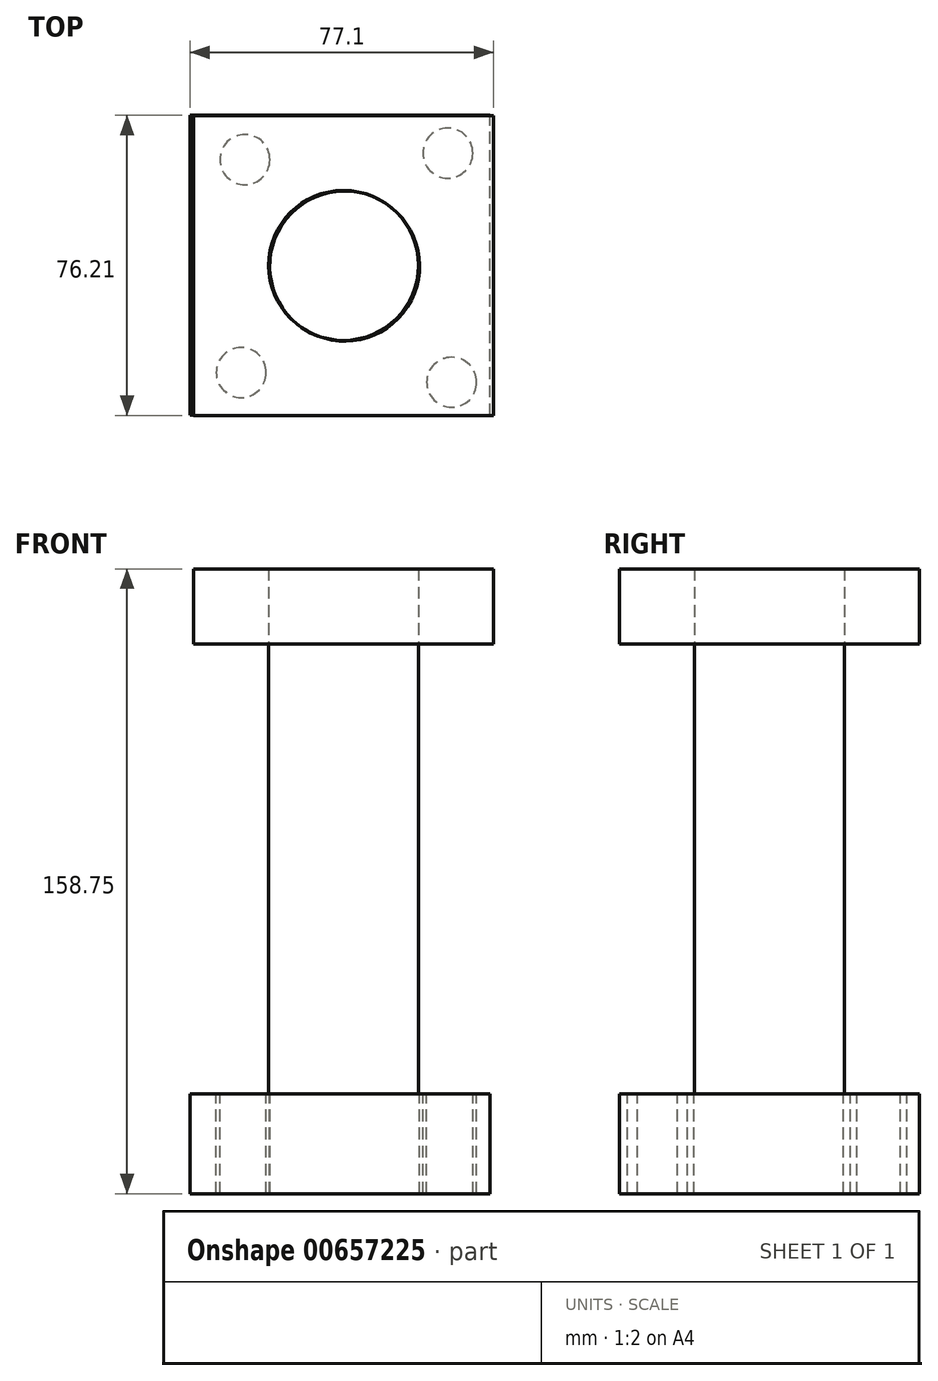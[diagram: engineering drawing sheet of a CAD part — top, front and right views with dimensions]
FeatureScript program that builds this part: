
annotation { "Feature Type Name" : "Feature", "Feature Type Description" : "" }
export const myFeature = defineFeature(function(context is Context, id is Id, definition is map)
    precondition{}
    {
        {
            var Q0;
            Q0=qCreatedBy(makeId("Top.planeOp"),FACE);
            var sketch = newSketch(context, id + "F0", { "sketchPlane" : qUnion([Q0])});
            skLineSegment(sketch, "E0.bottom", {"start": v(16.86, -50.22) * mm, "end": v(93.06, -50.22) * mm});
            skLineSegment(sketch, "E0.top", {"start": v(16.86, 25.98) * mm, "end": v(93.06, 25.98) * mm});
            skLineSegment(sketch, "E0.left", {"start": v(16.86, -50.22) * mm, "end": v(16.86, 25.98) * mm});
            skLineSegment(sketch, "E0.right", {"start": v(93.06, -50.22) * mm, "end": v(93.06, 25.98) * mm});
            skPoint(sketch, "E0.middle", {"position": v(54.96, -12.12) * mm});
            skSolve(sketch);
        }
        {
            var Q0;
            Q0 = qSketchRegion(id + "F0", true);
            extrude(context, id + "F1", {"entities" : qUnion([Q0]), "depth" : 25.4 * mm, "offsetDistance" : 25.4 * mm});
        }
        {
            var Q0;
            Q0=makeQuery(id+"F1.opExtrude","CAP_FACE",FACE,{"disambiguationData":[OSD([sQuery(id+"F0.wireOp",EDGE,"E0.bottom"),sQuery(id+"F0.wireOp",EDGE,"E0.top"),sQuery(id+"F0.wireOp",EDGE,"E0.left"),sQuery(id+"F0.wireOp",EDGE,"E0.right")])],"isStart":false});
            var sketch = newSketch(context, id + "F2", { "sketchPlane" : qUnion([Q0])});
            skCircle(sketch, "E1", {"center": v(56.15, -12.32) * mm, "radius": 19.05 * mm});
            skSolve(sketch);
        }
        {
            var Q0;
            Q0=makeQuery(id+"F2.imprint","IMPRINT",FACE,{"disambiguationData":[TD([[makeQuery(id+"F2.imprint","IMPRINT",EDGE,{"derivedFrom":sQuery(id+"F2.wireOp",EDGE,"E1")}),-1.0]])]});
            var sketch = newSketch(context, id + "F3", { "sketchPlane" : qUnion([Q0])});
            skSolve(sketch);
        }
        {
            var Q0;
            Q0=sQuery(id+"F2.wireOp",VERTEX,"E1.center");
            var Q1;
            Q1=makeQuery(id+"F1.opExtrude","SWEPT_BODY",BODY,{"disambiguationData":[OSD([sQuery(id+"F0.wireOp",EDGE,"E0.bottom"),sQuery(id+"F0.wireOp",EDGE,"E0.top"),sQuery(id+"F0.wireOp",EDGE,"E0.left"),sQuery(id+"F0.wireOp",EDGE,"E0.right")])]});
            hole(context, id + "F4", {"style" : HoleStyle.SIMPLE, "endStyle" : HoleEndStyle.THROUGH, "holeDiameter" : 38.1 * mm, "majorDiameter" : 6.35 * mm, "isTappedThrough" : true, "tappedDepth" : 12.7 * mm, "tapClearance" : 3, "locations" : qUnion([Q0]), "scope" : qUnion([Q1])});
        }
        {
            var Q0;
            Q0=makeQuery(id+"F3.imprint","IMPRINT",FACE,{"disambiguationData":[TD([[makeQuery(id+"F3.imprint","IMPRINT",EDGE,{"derivedFrom":makeQuery(id+"F2.imprint","IMPRINT",EDGE,{"derivedFrom":sQuery(id+"F2.wireOp",EDGE,"E1")})}),-1.0]])]});
            var sketch = newSketch(context, id + "F5", { "sketchPlane" : qUnion([Q0])});
            skCircle(sketch, "E2", {"center": v(82.35, 16.4) * mm, "radius": 4.88 * mm});
            skSolve(sketch);
        }
        {
            var Q0;
            Q0=makeQuery(id+"F5.imprint","IMPRINT",FACE,{"disambiguationData":[TD([[makeQuery(id+"F5.imprint","IMPRINT",EDGE,{"derivedFrom":sQuery(id+"F5.wireOp",EDGE,"E2")}),-1.0]])]});
            var sketch = newSketch(context, id + "F6", { "sketchPlane" : qUnion([Q0])});
            skCircle(sketch, "E3", {"center": v(83.35, -41.82) * mm, "radius": 4.75 * mm});
            skSolve(sketch);
        }
        {
            var Q0;
            Q0=makeQuery(id+"F3.imprint","IMPRINT",FACE,{"disambiguationData":[TD([[makeQuery(id+"F3.imprint","IMPRINT",EDGE,{"derivedFrom":makeQuery(id+"F2.imprint","IMPRINT",EDGE,{"derivedFrom":sQuery(id+"F2.wireOp",EDGE,"E1")})}),-1.0]])]});
            var sketch = newSketch(context, id + "F7", { "sketchPlane" : qUnion([Q0])});
            skCircle(sketch, "E4", {"center": v(29.88, -39.36) * mm, "radius": 5.21 * mm});
            skSolve(sketch);
        }
        {
            var Q0;
            Q0=makeQuery(id+"F3.imprint","IMPRINT",FACE,{"disambiguationData":[TD([[makeQuery(id+"F3.imprint","IMPRINT",EDGE,{"derivedFrom":makeQuery(id+"F2.imprint","IMPRINT",EDGE,{"derivedFrom":sQuery(id+"F2.wireOp",EDGE,"E1")})}),-1.0]])]});
            var sketch = newSketch(context, id + "F8", { "sketchPlane" : qUnion([Q0])});
            skCircle(sketch, "E5", {"center": v(30.8, 14.75) * mm, "radius": 4.7 * mm});
            skSolve(sketch);
        }
        {
            var Q0;
            Q0=sQuery(id+"F6.wireOp",VERTEX,"E3.center");
            var Q1;
            Q1=sQuery(id+"F7.wireOp",VERTEX,"E4.center");
            var Q2;
            Q2=sQuery(id+"F8.wireOp",VERTEX,"E5.center");
            var Q3;
            Q3=sQuery(id+"F5.wireOp",VERTEX,"E2.center");
            var Q4;
            Q4=makeQuery(id+"F1.opExtrude","SWEPT_BODY",BODY,{"disambiguationData":[OSD([sQuery(id+"F0.wireOp",EDGE,"E0.bottom"),sQuery(id+"F0.wireOp",EDGE,"E0.top"),sQuery(id+"F0.wireOp",EDGE,"E0.left"),sQuery(id+"F0.wireOp",EDGE,"E0.right")])]});
            hole(context, id + "F9", {"style" : HoleStyle.SIMPLE, "endStyle" : HoleEndStyle.THROUGH, "holeDiameter" : 12.7 * mm, "majorDiameter" : 6.35 * mm, "isTappedThrough" : true, "tappedDepth" : 12.7 * mm, "tapClearance" : 3, "locations" : qUnion([Q0, Q1, Q2, Q3]), "scope" : qUnion([Q4])});
        }
        {
            var Q0;
            Q0=makeQuery(id+"F3.imprint","IMPRINT",FACE,{"disambiguationData":[TD([[makeQuery(id+"F3.imprint","IMPRINT",EDGE,{"derivedFrom":makeQuery(id+"F2.imprint","IMPRINT",EDGE,{"derivedFrom":sQuery(id+"F2.wireOp",EDGE,"E1")})}),-1.0]])]});
            var sketch = newSketch(context, id + "F10", { "sketchPlane" : qUnion([Q0])});
            skCircle(sketch, "E6", {"center": v(55.86, -12.13) * mm, "radius": 19.05 * mm});
            skSolve(sketch);
        }
        {
            var Q0;
            Q0 = qSketchRegion(id + "F10", true);
            extrude(context, id + "F11", {"entities" : qUnion([Q0]), "operationType" : NewBodyOperationType.ADD, "depth" : 114.3 * mm, "offsetDistance" : 25.4 * mm});
        }
        {
            var Q0;
            Q0=makeQuery(id+"F11.opExtrude","CAP_FACE",FACE,{"disambiguationData":[OSD([sQuery(id+"F10.wireOp",EDGE,"E6")])],"isStart":false});
            var sketch = newSketch(context, id + "F12", { "sketchPlane" : qUnion([Q0])});
            skLineSegment(sketch, "E7.bottom", {"start": v(93.96, -50.23) * mm, "end": v(17.76, -50.23) * mm});
            skLineSegment(sketch, "E7.top", {"start": v(93.96, 25.97) * mm, "end": v(17.76, 25.97) * mm});
            skLineSegment(sketch, "E7.left", {"start": v(93.96, -50.23) * mm, "end": v(93.96, 25.97) * mm});
            skLineSegment(sketch, "E7.right", {"start": v(17.76, -50.23) * mm, "end": v(17.76, 25.97) * mm});
            skPoint(sketch, "E7.middle", {"position": v(55.86, -12.13) * mm});
            skSolve(sketch);
        }
        {
            var Q0;
            Q0=makeQuery(id+"F12.imprint","IMPRINT",FACE,{"disambiguationData":[TD([[makeQuery(id+"F12.imprint","IMPRINT",EDGE,{"derivedFrom":sQuery(id+"F12.wireOp",EDGE,"E7.bottom")}),-1.0]])]});
            extrude(context, id + "F13", {"entities" : qUnion([Q0]), "depth" : 25.4 * mm, "offsetDistance" : 25.4 * mm});
        }
        {
            var Q0;
            Q0=makeQuery(id+"F13.opExtrude","SWEPT_BODY",BODY,{"disambiguationData":[OSD([sQuery(id+"F10.wireOp",EDGE,"E6"),sQuery(id+"F12.wireOp",EDGE,"E7.bottom"),sQuery(id+"F12.wireOp",EDGE,"E7.top"),sQuery(id+"F12.wireOp",EDGE,"E7.left"),sQuery(id+"F12.wireOp",EDGE,"E7.right")])]});
            deleteBodies(context, id + "F14", {"entities" : qUnion([Q0])});
        }
        {
            var Q0;
            Q0=makeQuery(id+"F11.opExtrude","CAP_FACE",FACE,{"disambiguationData":[OSD([sQuery(id+"F10.wireOp",EDGE,"E6")])],"isStart":false});
            var sketch = newSketch(context, id + "F15", { "sketchPlane" : qUnion([Q0])});
            skLineSegment(sketch, "E8.bottom", {"start": v(17.76, -50.23) * mm, "end": v(93.96, -50.23) * mm});
            skLineSegment(sketch, "E8.top", {"start": v(17.76, 25.97) * mm, "end": v(93.96, 25.97) * mm});
            skLineSegment(sketch, "E8.left", {"start": v(17.76, -50.23) * mm, "end": v(17.76, 25.97) * mm});
            skLineSegment(sketch, "E8.right", {"start": v(93.96, -50.23) * mm, "end": v(93.96, 25.97) * mm});
            skPoint(sketch, "E8.middle", {"position": v(55.86, -12.13) * mm});
            skSolve(sketch);
        }
        {
            var Q0;
            Q0=makeQuery(id+"F15.imprint","IMPRINT",FACE,{"disambiguationData":[TD([[makeQuery(id+"F15.imprint","IMPRINT",EDGE,{"derivedFrom":sQuery(id+"F15.wireOp",EDGE,"E8.bottom")}),1.0]])]});
            extrude(context, id + "F16", {"entities" : qUnion([Q0]), "depth" : 19.05 * mm, "offsetDistance" : 25.4 * mm});
        }
    });
